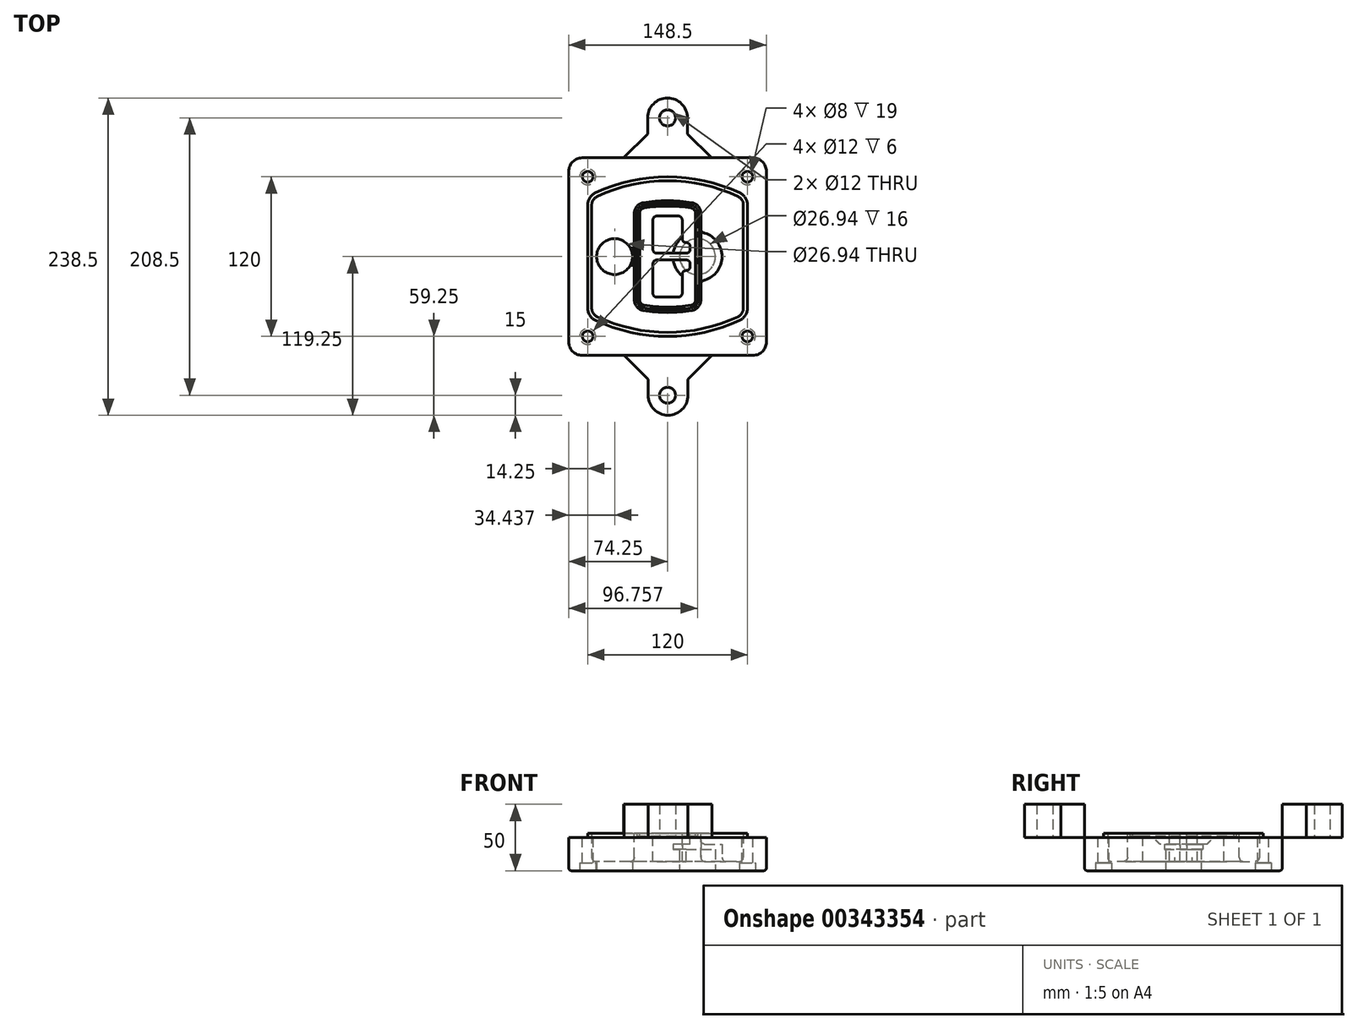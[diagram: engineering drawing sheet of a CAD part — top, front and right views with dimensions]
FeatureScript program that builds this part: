
annotation { "Feature Type Name" : "Feature", "Feature Type Description" : "" }
export const myFeature = defineFeature(function(context is Context, id is Id, definition is map)
    precondition{}
    {
        {
            var Q0;
            Q0=qCreatedBy(makeId("Top.planeOp"),FACE);
            var sketch = newSketch(context, id + "F0", { "sketchPlane" : qUnion([Q0])});
            skPoint(sketch, "E0.rect.middle", {"position": v(0, 0) * mm});
            skLineSegment(sketch, "E1.bottom", {"start": v(-64.25, -74.25) * mm, "end": v(64.25, -74.25) * mm});
            skLineSegment(sketch, "E1.top", {"start": v(-64.25, 74.25) * mm, "end": v(64.25, 74.25) * mm});
            skLineSegment(sketch, "E1.left", {"start": v(-74.25, -64.25) * mm, "end": v(-74.25, 64.25) * mm});
            skLineSegment(sketch, "E1.right", {"start": v(74.25, -64.25) * mm, "end": v(74.25, 64.25) * mm});
            skLineSegment(sketch, "E2", {"start": v(-74.25, 74.25) * mm, "end": v(74.25, -74.25) * mm, "construction": true});
            skLineSegment(sketch, "E3", {"start": v(74.25, 74.25) * mm, "end": v(-74.25, -74.25) * mm, "construction": true});
            skCircle(sketch, "E4", {"center": v(-60, 60) * mm, "radius": 4 * mm});
            skCircle(sketch, "E5", {"center": v(60, 60) * mm, "radius": 4 * mm});
            skCircle(sketch, "E6", {"center": v(60, -60) * mm, "radius": 4 * mm});
            skCircle(sketch, "E7", {"center": v(-60, -60) * mm, "radius": 4 * mm});
            skLineSegment(sketch, "E8", {"start": v(-60, 60) * mm, "end": v(60, 60) * mm, "construction": true});
            skLineSegment(sketch, "E9", {"start": v(60, 60) * mm, "end": v(60, -60) * mm, "construction": true});
            skLineSegment(sketch, "E10", {"start": v(60, -60) * mm, "end": v(-60, -60) * mm, "construction": true});
            skLineSegment(sketch, "E11", {"start": v(-60, -60) * mm, "end": v(-60, 60) * mm, "construction": true});
            skLineSegment(sketch, "E12", {"start": v(-60, 38.83) * mm, "end": v(-60, -38.83) * mm});
            skLineSegment(sketch, "E13", {"start": v(60, 38.83) * mm, "end": v(60, -38.83) * mm});
            skArc(sketch, "E14", {"start": v(54.26, 47.88) * mm, "mid": v(0, 60) * mm, "end": v(-54.26, 47.88) * mm});
            skArc(sketch, "E15", {"start": v(-54.26, -47.88) * mm, "mid": v(0, -60) * mm, "end": v(54.26, -47.88) * mm});
            skLineSegment(sketch, "E16", {"start": v(-60, 0) * mm, "end": v(60, 0) * mm, "construction": true});
            skPoint(sketch, "E17.visualSharp", {"position": v(-60, -45) * mm});
            skArc(sketch, "E17.filletArc", {"start": v(-60, -38.83) * mm, "mid": v(-58.44, -44.2) * mm, "end": v(-54.26, -47.88) * mm});
            skPoint(sketch, "E18.visualSharp", {"position": v(-60, 45) * mm});
            skArc(sketch, "E18.filletArc", {"start": v(-54.26, 47.88) * mm, "mid": v(-58.44, 44.2) * mm, "end": v(-60, 38.83) * mm});
            skPoint(sketch, "E19.visualSharp", {"position": v(60, 45) * mm});
            skArc(sketch, "E19.filletArc", {"start": v(60, 38.83) * mm, "mid": v(58.44, 44.2) * mm, "end": v(54.26, 47.88) * mm});
            skPoint(sketch, "E20.visualSharp", {"position": v(60, -45) * mm});
            skArc(sketch, "E20.filletArc", {"start": v(54.26, -47.88) * mm, "mid": v(58.44, -44.2) * mm, "end": v(60, -38.83) * mm});
            skPoint(sketch, "E21.visualSharp", {"position": v(-74.25, 74.25) * mm});
            skArc(sketch, "E21.filletArc", {"start": v(-64.25, 74.25) * mm, "mid": v(-71.32, 71.32) * mm, "end": v(-74.25, 64.25) * mm});
            skPoint(sketch, "E22.visualSharp", {"position": v(74.25, 74.25) * mm});
            skArc(sketch, "E22.filletArc", {"start": v(74.25, 64.25) * mm, "mid": v(71.32, 71.32) * mm, "end": v(64.25, 74.25) * mm});
            skPoint(sketch, "E23.visualSharp", {"position": v(74.25, -74.25) * mm});
            skArc(sketch, "E23.filletArc", {"start": v(64.25, -74.25) * mm, "mid": v(71.32, -71.32) * mm, "end": v(74.25, -64.25) * mm});
            skPoint(sketch, "E24.visualSharp", {"position": v(-74.25, -74.25) * mm});
            skArc(sketch, "E24.filletArc", {"start": v(-74.25, -64.25) * mm, "mid": v(-71.32, -71.32) * mm, "end": v(-64.25, -74.25) * mm});
            skArc(sketch, "E25.0", {"start": v(57, 38.83) * mm, "mid": v(55.9, 42.58) * mm, "end": v(52.98, 45.17) * mm});
            skLineSegment(sketch, "E25.1", {"start": v(57, 38.83) * mm, "end": v(57, -38.83) * mm});
            skArc(sketch, "E25.2", {"start": v(52.98, -45.17) * mm, "mid": v(55.9, -42.58) * mm, "end": v(57, -38.83) * mm});
            skArc(sketch, "E25.3", {"start": v(-52.98, -45.17) * mm, "mid": v(0, -57) * mm, "end": v(52.98, -45.17) * mm});
            skArc(sketch, "E25.4", {"start": v(-57, -38.83) * mm, "mid": v(-55.9, -42.58) * mm, "end": v(-52.98, -45.17) * mm});
            skArc(sketch, "E25.5", {"start": v(52.98, 45.17) * mm, "mid": v(0, 57) * mm, "end": v(-52.98, 45.17) * mm});
            skLineSegment(sketch, "E25.6", {"start": v(-57, 38.83) * mm, "end": v(-57, -38.83) * mm});
            skArc(sketch, "E25.7", {"start": v(-52.98, 45.17) * mm, "mid": v(-55.9, 42.58) * mm, "end": v(-57, 38.83) * mm});
            skArc(sketch, "E26.0", {"start": v(-55.96, 51.5) * mm, "mid": v(-61.82, 46.33) * mm, "end": v(-64, 38.83) * mm});
            skArc(sketch, "E26.1", {"start": v(55.96, 51.5) * mm, "mid": v(0, 64) * mm, "end": v(-55.96, 51.5) * mm});
            skArc(sketch, "E26.2", {"start": v(64, 38.83) * mm, "mid": v(61.82, 46.33) * mm, "end": v(55.96, 51.5) * mm});
            skLineSegment(sketch, "E26.3", {"start": v(64, 38.83) * mm, "end": v(64, -38.83) * mm});
            skArc(sketch, "E26.4", {"start": v(55.96, -51.5) * mm, "mid": v(61.82, -46.33) * mm, "end": v(64, -38.83) * mm});
            skLineSegment(sketch, "E26.5", {"start": v(-64, 38.83) * mm, "end": v(-64, -38.83) * mm});
            skArc(sketch, "E26.6", {"start": v(-55.96, -51.5) * mm, "mid": v(0, -64) * mm, "end": v(55.96, -51.5) * mm});
            skArc(sketch, "E26.7", {"start": v(-64, -38.83) * mm, "mid": v(-61.82, -46.33) * mm, "end": v(-55.96, -51.5) * mm});
            skSolve(sketch);
        }
        {
            var Q0;
            Q0=makeQuery(id+"F0.imprint","IMPRINT",FACE,{"disambiguationData":[TD([[makeQuery(id+"F0.imprint","IMPRINT",EDGE,{"derivedFrom":sQuery(id+"F0.wireOp",EDGE,"E1.bottom")}),1.0]])]});
            var Q1;
            Q1=makeQuery(id+"F0.imprint","IMPRINT",FACE,{"disambiguationData":[TD([[makeQuery(id+"F0.imprint","IMPRINT",EDGE,{"derivedFrom":sQuery(id+"F0.wireOp",EDGE,"E12")}),1.0]])]});
            var Q2;
            Q2=makeQuery(id+"F0.imprint","IMPRINT",FACE,{"disambiguationData":[TD([[makeQuery(id+"F0.imprint","IMPRINT",EDGE,{"derivedFrom":sQuery(id+"F0.wireOp",EDGE,"E25.0")}),1.0]])]});
            var Q3;
            Q3=makeQuery(id+"F0.imprint","IMPRINT",FACE,{"disambiguationData":[TD([[makeQuery(id+"F0.imprint","IMPRINT",EDGE,{"derivedFrom":sQuery(id+"F0.wireOp",EDGE,"E12")}),-1.0]])]});
            extrude(context, id + "F1", {"entities" : qUnion([Q0, Q1, Q2, Q3]), "oppositeDirection" : true, "depth" : 25 * mm});
        }
        {
            var Q0;
            Q0=makeQuery(id+"F0.imprint","IMPRINT",FACE,{"disambiguationData":[TD([[makeQuery(id+"F0.imprint","IMPRINT",EDGE,{"derivedFrom":sQuery(id+"F0.wireOp",EDGE,"E12")}),1.0]])]});
            extrude(context, id + "F2", {"entities" : qUnion([Q0]), "operationType" : NewBodyOperationType.ADD, "depth" : 3 * mm});
        }
        {
            var Q0;
            Q0=makeQuery(id+"F0.imprint","IMPRINT",FACE,{"disambiguationData":[TD([[makeQuery(id+"F0.imprint","IMPRINT",EDGE,{"derivedFrom":sQuery(id+"F0.wireOp",EDGE,"E25.0")}),1.0]])]});
            extrude(context, id + "F3", {"entities" : qUnion([Q0]), "operationType" : NewBodyOperationType.REMOVE, "oppositeDirection" : true, "depth" : 18 * mm});
        }
        {
            var Q0;
            Q0=makeQuery(id+"F2.opExtrude","CAP_FACE",FACE,{"disambiguationData":[OSD([sQuery(id+"F0.wireOp",EDGE,"E12"),sQuery(id+"F0.wireOp",EDGE,"E13"),sQuery(id+"F0.wireOp",EDGE,"E14"),sQuery(id+"F0.wireOp",EDGE,"E15"),sQuery(id+"F0.wireOp",EDGE,"E17.filletArc"),sQuery(id+"F0.wireOp",EDGE,"E18.filletArc"),sQuery(id+"F0.wireOp",EDGE,"E19.filletArc"),sQuery(id+"F0.wireOp",EDGE,"E20.filletArc"),sQuery(id+"F0.wireOp",EDGE,"E25.0"),sQuery(id+"F0.wireOp",EDGE,"E25.1"),sQuery(id+"F0.wireOp",EDGE,"E25.2"),sQuery(id+"F0.wireOp",EDGE,"E25.3"),sQuery(id+"F0.wireOp",EDGE,"E25.4"),sQuery(id+"F0.wireOp",EDGE,"E25.5"),sQuery(id+"F0.wireOp",EDGE,"E25.6"),sQuery(id+"F0.wireOp",EDGE,"E25.7")])],"isStart":false});
            var sketch = newSketch(context, id + "F4", { "sketchPlane" : qUnion([Q0])});
            skArc(sketch, "E27.0", {"start": v(-18.34, -40.45) * mm, "mid": v(0, -42) * mm, "end": v(18.34, -40.45) * mm});
            skArc(sketch, "E28.0", {"start": v(18.34, 40.45) * mm, "mid": v(0, 42) * mm, "end": v(-18.34, 40.45) * mm});
            skLineSegment(sketch, "E29", {"start": v(-25, 32.57) * mm, "end": v(-25, -32.57) * mm});
            skLineSegment(sketch, "E30", {"start": v(25, 32.57) * mm, "end": v(25, -32.57) * mm});
            skLineSegment(sketch, "E31", {"start": v(-25, 39.1) * mm, "end": v(25, 39.1) * mm, "construction": true});
            skLineSegment(sketch, "E32", {"start": v(-25, -39.1) * mm, "end": v(25, -39.1) * mm, "construction": true});
            skPoint(sketch, "E33.visualSharp", {"position": v(-25, 39.1) * mm});
            skArc(sketch, "E33.filletArc", {"start": v(-18.34, 40.45) * mm, "mid": v(-23.11, 37.73) * mm, "end": v(-25, 32.57) * mm});
            skPoint(sketch, "E34.visualSharp", {"position": v(25, 39.1) * mm});
            skArc(sketch, "E34.filletArc", {"start": v(25, 32.57) * mm, "mid": v(23.11, 37.73) * mm, "end": v(18.34, 40.45) * mm});
            skPoint(sketch, "E35.visualSharp", {"position": v(25, -39.1) * mm});
            skArc(sketch, "E35.filletArc", {"start": v(18.34, -40.45) * mm, "mid": v(23.11, -37.73) * mm, "end": v(25, -32.57) * mm});
            skPoint(sketch, "E36.visualSharp", {"position": v(-25, -39.1) * mm});
            skArc(sketch, "E36.filletArc", {"start": v(-25, -32.57) * mm, "mid": v(-23.11, -37.73) * mm, "end": v(-18.34, -40.45) * mm});
            skArc(sketch, "E37.0", {"start": v(52.98, 45.17) * mm, "mid": v(0, 57) * mm, "end": v(-52.98, 45.17) * mm});
            skArc(sketch, "E37.1", {"start": v(-52.98, 45.17) * mm, "mid": v(-55.9, 42.58) * mm, "end": v(-57, 38.83) * mm});
            skLineSegment(sketch, "E37.2", {"start": v(-57, 38.83) * mm, "end": v(-57, -38.83) * mm});
            skArc(sketch, "E37.3", {"start": v(-57, -38.83) * mm, "mid": v(-55.9, -42.58) * mm, "end": v(-52.98, -45.17) * mm});
            skArc(sketch, "E37.4", {"start": v(-52.98, -45.17) * mm, "mid": v(0, -57) * mm, "end": v(52.98, -45.17) * mm});
            skArc(sketch, "E37.5", {"start": v(52.98, -45.17) * mm, "mid": v(55.9, -42.58) * mm, "end": v(57, -38.83) * mm});
            skLineSegment(sketch, "E37.6", {"start": v(57, 38.83) * mm, "end": v(57, -38.83) * mm});
            skArc(sketch, "E37.7", {"start": v(57, 38.83) * mm, "mid": v(55.9, 42.58) * mm, "end": v(52.98, 45.17) * mm});
            skLineSegment(sketch, "E38.0", {"start": v(23, 32.57) * mm, "end": v(23, -32.57) * mm});
            skArc(sketch, "E38.1", {"start": v(18, -38.48) * mm, "mid": v(21.58, -36.44) * mm, "end": v(23, -32.57) * mm});
            skArc(sketch, "E38.2", {"start": v(-18, -38.48) * mm, "mid": v(0, -40) * mm, "end": v(18, -38.48) * mm});
            skArc(sketch, "E38.3", {"start": v(-23, -32.57) * mm, "mid": v(-21.58, -36.44) * mm, "end": v(-18, -38.48) * mm});
            skLineSegment(sketch, "E38.4", {"start": v(-23, 32.57) * mm, "end": v(-23, -32.57) * mm});
            skArc(sketch, "E38.5", {"start": v(23, 32.57) * mm, "mid": v(21.58, 36.44) * mm, "end": v(18, 38.48) * mm});
            skArc(sketch, "E38.6", {"start": v(-18, 38.48) * mm, "mid": v(-21.58, 36.44) * mm, "end": v(-23, 32.57) * mm});
            skArc(sketch, "E38.7", {"start": v(18, 38.48) * mm, "mid": v(0, 40) * mm, "end": v(-18, 38.48) * mm});
            skArc(sketch, "E39.0", {"start": v(21, 32.57) * mm, "mid": v(20.06, 35.15) * mm, "end": v(17.67, 36.5) * mm});
            skLineSegment(sketch, "E39.1", {"start": v(21, 32.57) * mm, "end": v(21, -32.57) * mm});
            skArc(sketch, "E39.2", {"start": v(17.67, -36.5) * mm, "mid": v(20.06, -35.15) * mm, "end": v(21, -32.57) * mm});
            skArc(sketch, "E39.3", {"start": v(-17.67, -36.5) * mm, "mid": v(0, -38) * mm, "end": v(17.67, -36.5) * mm});
            skArc(sketch, "E39.4", {"start": v(-21, -32.57) * mm, "mid": v(-20.06, -35.15) * mm, "end": v(-17.67, -36.5) * mm});
            skArc(sketch, "E39.5", {"start": v(17.67, 36.5) * mm, "mid": v(0, 38) * mm, "end": v(-17.67, 36.5) * mm});
            skLineSegment(sketch, "E39.6", {"start": v(-21, 32.57) * mm, "end": v(-21, -32.57) * mm});
            skArc(sketch, "E39.7", {"start": v(-17.67, 36.5) * mm, "mid": v(-20.06, 35.15) * mm, "end": v(-21, 32.57) * mm});
            skLineSegment(sketch, "E40", {"start": v(-25, 0) * mm, "end": v(25, 0) * mm, "construction": true});
            skLineSegment(sketch, "E41", {"start": v(-11, 5.5) * mm, "end": v(-11, 27.5) * mm});
            skLineSegment(sketch, "E42", {"start": v(-8, 30.5) * mm, "end": v(8, 30.5) * mm});
            skLineSegment(sketch, "E43", {"start": v(11, 27.5) * mm, "end": v(11, 13.5) * mm});
            skLineSegment(sketch, "E44", {"start": v(14, 10.5) * mm, "end": v(14, 10.5) * mm});
            skLineSegment(sketch, "E45", {"start": v(17, 7.5) * mm, "end": v(17, 5.5) * mm});
            skLineSegment(sketch, "E46", {"start": v(14, 2.5) * mm, "end": v(-8, 2.5) * mm});
            skPoint(sketch, "E47.visualSharp", {"position": v(-11, 30.5) * mm});
            skArc(sketch, "E47.filletArc", {"start": v(-8, 30.5) * mm, "mid": v(-10.12, 29.62) * mm, "end": v(-11, 27.5) * mm});
            skPoint(sketch, "E48.visualSharp", {"position": v(11, 30.5) * mm});
            skArc(sketch, "E48.filletArc", {"start": v(11, 27.5) * mm, "mid": v(10.12, 29.62) * mm, "end": v(8, 30.5) * mm});
            skPoint(sketch, "E49.visualSharp", {"position": v(11, 10.5) * mm});
            skArc(sketch, "E49.filletArc", {"start": v(11, 13.5) * mm, "mid": v(11.88, 11.38) * mm, "end": v(14, 10.5) * mm});
            skPoint(sketch, "E50.visualSharp", {"position": v(17, 10.5) * mm});
            skArc(sketch, "E50.filletArc", {"start": v(17, 7.5) * mm, "mid": v(16.12, 9.62) * mm, "end": v(14, 10.5) * mm});
            skPoint(sketch, "E51.visualSharp", {"position": v(17, 2.5) * mm});
            skArc(sketch, "E51.filletArc", {"start": v(14, 2.5) * mm, "mid": v(16.12, 3.38) * mm, "end": v(17, 5.5) * mm});
            skPoint(sketch, "E52.visualSharp", {"position": v(-11, 2.5) * mm});
            skArc(sketch, "E52.filletArc", {"start": v(-11, 5.5) * mm, "mid": v(-10.12, 3.38) * mm, "end": v(-8, 2.5) * mm});
            skLineSegment(sketch, "E53.0.MirrorCS", {"start": v(14, -2.5) * mm, "end": v(-8, -2.5) * mm});
            skArc(sketch, "E54.0.MirrorCS", {"start": v(-11, -5.5) * mm, "mid": v(-10.12, -3.38) * mm, "end": v(-8, -2.5) * mm});
            skLineSegment(sketch, "E55.0.MirrorCS", {"start": v(-11, -5.5) * mm, "end": v(-11, -27.5) * mm});
            skArc(sketch, "E56.0.MirrorCS", {"start": v(-8, -30.5) * mm, "mid": v(-10.12, -29.62) * mm, "end": v(-11, -27.5) * mm});
            skLineSegment(sketch, "E57.0.MirrorCS", {"start": v(-8, -30.5) * mm, "end": v(8, -30.5) * mm});
            skArc(sketch, "E58.0.MirrorCS", {"start": v(11, -27.5) * mm, "mid": v(10.12, -29.62) * mm, "end": v(8, -30.5) * mm});
            skLineSegment(sketch, "E59.0.MirrorCS", {"start": v(11, -27.5) * mm, "end": v(11, -13.5) * mm});
            skArc(sketch, "E60.0.MirrorCS", {"start": v(11, -13.5) * mm, "mid": v(11.88, -11.38) * mm, "end": v(14, -10.5) * mm});
            skArc(sketch, "E61.0.MirrorCS", {"start": v(17, -7.5) * mm, "mid": v(16.12, -9.62) * mm, "end": v(14, -10.5) * mm});
            skLineSegment(sketch, "E62.0.MirrorCS", {"start": v(17, -7.5) * mm, "end": v(17, -5.5) * mm});
            skArc(sketch, "E63.0.MirrorCS", {"start": v(14, -2.5) * mm, "mid": v(16.12, -3.38) * mm, "end": v(17, -5.5) * mm});
            skSolve(sketch);
        }
        {
            var Q0;
            Q0=makeQuery(id+"F4.imprint","IMPRINT",FACE,{"disambiguationData":[TD([[makeQuery(id+"F4.imprint","IMPRINT",EDGE,{"derivedFrom":sQuery(id+"F4.wireOp",EDGE,"E27.0")}),1.0]])]});
            var Q1;
            Q1=makeQuery(id+"F4.imprint","IMPRINT",FACE,{"disambiguationData":[TD([[makeQuery(id+"F4.imprint","IMPRINT",EDGE,{"derivedFrom":sQuery(id+"F4.wireOp",EDGE,"E38.0")}),-1.0]])]});
            var Q2;
            Q2=makeQuery(id+"F4.imprint","IMPRINT",FACE,{"disambiguationData":[TD([[makeQuery(id+"F4.imprint","IMPRINT",EDGE,{"derivedFrom":sQuery(id+"F4.wireOp",EDGE,"E39.0")}),1.0]])]});
            extrude(context, id + "F5", {"entities" : qUnion([Q0, Q1, Q2]), "operationType" : NewBodyOperationType.ADD, "endBound" : BoundingType.UP_TO_NEXT, "oppositeDirection" : true, "depth" : 25 * mm});
        }
        {
            var Q0;
            Q0=makeQuery(id+"F4.imprint","IMPRINT",FACE,{"disambiguationData":[TD([[makeQuery(id+"F4.imprint","IMPRINT",EDGE,{"derivedFrom":sQuery(id+"F4.wireOp",EDGE,"E38.0")}),-1.0]])]});
            extrude(context, id + "F6", {"entities" : qUnion([Q0]), "operationType" : NewBodyOperationType.REMOVE, "oppositeDirection" : true, "depth" : 2 * mm});
        }
        {
            var Q0;
            Q0=makeQuery(id+"F1.opExtrude","CAP_FACE",FACE,{"disambiguationData":[OSD([sQuery(id+"F0.wireOp",EDGE,"E1.bottom"),sQuery(id+"F0.wireOp",EDGE,"E1.top"),sQuery(id+"F0.wireOp",EDGE,"E1.left"),sQuery(id+"F0.wireOp",EDGE,"E1.right"),sQuery(id+"F0.wireOp",EDGE,"E4"),sQuery(id+"F0.wireOp",EDGE,"E5"),sQuery(id+"F0.wireOp",EDGE,"E6"),sQuery(id+"F0.wireOp",EDGE,"E7"),sQuery(id+"F0.wireOp",EDGE,"E21.filletArc"),sQuery(id+"F0.wireOp",EDGE,"E22.filletArc"),sQuery(id+"F0.wireOp",EDGE,"E23.filletArc"),sQuery(id+"F0.wireOp",EDGE,"E24.filletArc")])],"isStart":false});
            var sketch = newSketch(context, id + "F7", { "sketchPlane" : qUnion([Q0])});
            skCircle(sketch, "E64", {"center": v(22.5, 0) * mm, "radius": 13.47 * mm});
            skCircle(sketch, "E65", {"center": v(-39.81, 0) * mm, "radius": 13.47 * mm});
            skLineSegment(sketch, "E66", {"start": v(74.25, 0) * mm, "end": v(-74.25, 0) * mm});
            skCircle(sketch, "E67", {"center": v(22.5, 0) * mm, "radius": 18.47 * mm});
            skCircle(sketch, "E68", {"center": v(60, -60) * mm, "radius": 6 * mm});
            skCircle(sketch, "E69", {"center": v(-60, -60) * mm, "radius": 6 * mm});
            skCircle(sketch, "E70", {"center": v(-60, 60) * mm, "radius": 6 * mm});
            skCircle(sketch, "E71", {"center": v(60, 60) * mm, "radius": 6 * mm});
            skSolve(sketch);
        }
        {
            var Q0;
            {var subQ1=sQuery(id+"F7.wireOp",EDGE,"E66");var subQ4=sQuery(id+"F7.wireOp",EDGE,"E64");var subQ6=makeQuery(id+"F7.imprint","INTERSECT",VERTEX,{"disambiguationData":[OD(0.0)],"derivedFrom":[subQ4,subQ1]});Q0=makeQuery(id+"F7.imprint","IMPRINT",FACE,{"disambiguationData":[TD([[makeQuery(id+"F7.imprint","IMPRINT",EDGE,{"disambiguationData":[TD([[subQ6,-1.0]])],"derivedFrom":subQ4}),-1.0]])]});}
            var Q1;
            {var subQ0=sQuery(id+"F7.wireOp",EDGE,"E66");var subQ1=sQuery(id+"F7.wireOp",EDGE,"E64");var subQ3=makeQuery(id+"F7.imprint","INTERSECT",VERTEX,{"disambiguationData":[OD(0.0)],"derivedFrom":[subQ1,subQ0]});Q1=makeQuery(id+"F7.imprint","IMPRINT",FACE,{"disambiguationData":[TD([[makeQuery(id+"F7.imprint","IMPRINT",EDGE,{"disambiguationData":[TD([[subQ3,-1.0]])],"derivedFrom":subQ1}),1.0]])]});}
            var Q2;
            {var subQ0=sQuery(id+"F7.wireOp",EDGE,"E66");var subQ1=sQuery(id+"F7.wireOp",EDGE,"E64");var subQ3=makeQuery(id+"F7.imprint","INTERSECT",VERTEX,{"disambiguationData":[OD(0.0)],"derivedFrom":[subQ1,subQ0]});Q2=makeQuery(id+"F7.imprint","IMPRINT",FACE,{"disambiguationData":[TD([[makeQuery(id+"F7.imprint","IMPRINT",EDGE,{"disambiguationData":[TD([[subQ3,1.0]])],"derivedFrom":subQ1}),1.0]])]});}
            var Q3;
            {var subQ1=sQuery(id+"F7.wireOp",EDGE,"E66");var subQ4=sQuery(id+"F7.wireOp",EDGE,"E64");var subQ6=makeQuery(id+"F7.imprint","INTERSECT",VERTEX,{"disambiguationData":[OD(0.0)],"derivedFrom":[subQ4,subQ1]});Q3=makeQuery(id+"F7.imprint","IMPRINT",FACE,{"disambiguationData":[TD([[makeQuery(id+"F7.imprint","IMPRINT",EDGE,{"disambiguationData":[TD([[subQ6,1.0]])],"derivedFrom":subQ4}),-1.0]])]});}
            extrude(context, id + "F8", {"entities" : qUnion([Q0, Q1, Q2, Q3]), "operationType" : NewBodyOperationType.ADD, "oppositeDirection" : true, "depth" : 20 * mm});
        }
        {
            var Q0;
            {var subQ0=sQuery(id+"F7.wireOp",EDGE,"E66");var subQ1=sQuery(id+"F7.wireOp",EDGE,"E64");var subQ3=makeQuery(id+"F7.imprint","INTERSECT",VERTEX,{"disambiguationData":[OD(0.0)],"derivedFrom":[subQ1,subQ0]});Q0=makeQuery(id+"F7.imprint","IMPRINT",FACE,{"disambiguationData":[TD([[makeQuery(id+"F7.imprint","IMPRINT",EDGE,{"disambiguationData":[TD([[subQ3,-1.0]])],"derivedFrom":subQ1}),1.0]])]});}
            var Q1;
            {var subQ0=sQuery(id+"F7.wireOp",EDGE,"E66");var subQ1=sQuery(id+"F7.wireOp",EDGE,"E64");var subQ3=makeQuery(id+"F7.imprint","INTERSECT",VERTEX,{"disambiguationData":[OD(0.0)],"derivedFrom":[subQ1,subQ0]});Q1=makeQuery(id+"F7.imprint","IMPRINT",FACE,{"disambiguationData":[TD([[makeQuery(id+"F7.imprint","IMPRINT",EDGE,{"disambiguationData":[TD([[subQ3,1.0]])],"derivedFrom":subQ1}),1.0]])]});}
            extrude(context, id + "F9", {"entities" : qUnion([Q0, Q1]), "operationType" : NewBodyOperationType.REMOVE, "oppositeDirection" : true, "depth" : 16 * mm});
        }
        {
            var Q0;
            {var subQ0=sQuery(id+"F7.wireOp",EDGE,"E66");var subQ1=sQuery(id+"F7.wireOp",EDGE,"E65");var subQ3=makeQuery(id+"F7.imprint","INTERSECT",VERTEX,{"disambiguationData":[OD(0.0)],"derivedFrom":[subQ1,subQ0]});Q0=makeQuery(id+"F7.imprint","IMPRINT",FACE,{"disambiguationData":[TD([[makeQuery(id+"F7.imprint","IMPRINT",EDGE,{"disambiguationData":[TD([[subQ3,-1.0]])],"derivedFrom":subQ1}),1.0]])]});}
            var Q1;
            {var subQ0=sQuery(id+"F7.wireOp",EDGE,"E66");var subQ1=sQuery(id+"F7.wireOp",EDGE,"E65");var subQ3=makeQuery(id+"F7.imprint","INTERSECT",VERTEX,{"disambiguationData":[OD(0.0)],"derivedFrom":[subQ1,subQ0]});Q1=makeQuery(id+"F7.imprint","IMPRINT",FACE,{"disambiguationData":[TD([[makeQuery(id+"F7.imprint","IMPRINT",EDGE,{"disambiguationData":[TD([[subQ3,1.0]])],"derivedFrom":subQ1}),1.0]])]});}
            extrude(context, id + "F10", {"entities" : qUnion([Q0, Q1]), "operationType" : NewBodyOperationType.REMOVE, "oppositeDirection" : true, "depth" : 25 * mm});
        }
        {
            var Q0;
            Q0=makeQuery(id+"F7.imprint","IMPRINT",FACE,{"disambiguationData":[TD([[makeQuery(id+"F7.imprint","IMPRINT",EDGE,{"derivedFrom":sQuery(id+"F7.wireOp",EDGE,"E68")}),1.0]])]});
            var Q1;
            Q1=makeQuery(id+"F7.imprint","IMPRINT",FACE,{"disambiguationData":[TD([[makeQuery(id+"F7.imprint","IMPRINT",EDGE,{"derivedFrom":makeQuery(id+"F1.opExtrude","CAP_EDGE",EDGE,{"disambiguationData":[OSD([sQuery(id+"F0.wireOp",EDGE,"E5")])],"isStart":false})}),-1.0]])]});
            var Q2;
            Q2=makeQuery(id+"F7.imprint","IMPRINT",FACE,{"disambiguationData":[TD([[makeQuery(id+"F7.imprint","IMPRINT",EDGE,{"derivedFrom":sQuery(id+"F7.wireOp",EDGE,"E69")}),1.0]])]});
            var Q3;
            Q3=makeQuery(id+"F7.imprint","IMPRINT",FACE,{"disambiguationData":[TD([[makeQuery(id+"F7.imprint","IMPRINT",EDGE,{"derivedFrom":makeQuery(id+"F1.opExtrude","CAP_EDGE",EDGE,{"disambiguationData":[OSD([sQuery(id+"F0.wireOp",EDGE,"E4")])],"isStart":false})}),-1.0]])]});
            var Q4;
            Q4=makeQuery(id+"F7.imprint","IMPRINT",FACE,{"disambiguationData":[TD([[makeQuery(id+"F7.imprint","IMPRINT",EDGE,{"derivedFrom":sQuery(id+"F7.wireOp",EDGE,"E70")}),1.0]])]});
            var Q5;
            Q5=makeQuery(id+"F7.imprint","IMPRINT",FACE,{"disambiguationData":[TD([[makeQuery(id+"F7.imprint","IMPRINT",EDGE,{"derivedFrom":makeQuery(id+"F1.opExtrude","CAP_EDGE",EDGE,{"disambiguationData":[OSD([sQuery(id+"F0.wireOp",EDGE,"E7")])],"isStart":false})}),-1.0]])]});
            var Q6;
            Q6=makeQuery(id+"F7.imprint","IMPRINT",FACE,{"disambiguationData":[TD([[makeQuery(id+"F7.imprint","IMPRINT",EDGE,{"derivedFrom":sQuery(id+"F7.wireOp",EDGE,"E71")}),1.0]])]});
            var Q7;
            Q7=makeQuery(id+"F7.imprint","IMPRINT",FACE,{"disambiguationData":[TD([[makeQuery(id+"F7.imprint","IMPRINT",EDGE,{"derivedFrom":makeQuery(id+"F1.opExtrude","CAP_EDGE",EDGE,{"disambiguationData":[OSD([sQuery(id+"F0.wireOp",EDGE,"E6")])],"isStart":false})}),-1.0]])]});
            extrude(context, id + "F11", {"entities" : qUnion([Q0, Q1, Q2, Q3, Q4, Q5, Q6, Q7]), "operationType" : NewBodyOperationType.REMOVE, "oppositeDirection" : true, "depth" : 6 * mm});
        }
        {
            var Q0;
            Q0=makeQuery(id+"F9.boolean.opBoolean","COPY",FACE,{"derivedFrom":makeQuery(id+"F9.opExtrude","CAP_FACE",FACE,{"disambiguationData":[OSD([sQuery(id+"F7.wireOp",EDGE,"E64")])],"isStart":false})});
            var sketch = newSketch(context, id + "F12", { "sketchPlane" : qUnion([Q0])});
            skArc(sketch, "E72.0", {"start": v(11, 14.45) * mm, "mid": v(6.45, 9.13) * mm, "end": v(4.2, 2.5) * mm});
            skArc(sketch, "E72.1", {"start": v(4.2, -2.5) * mm, "mid": v(6.45, -9.13) * mm, "end": v(11, -14.45) * mm});
            skLineSegment(sketch, "E73", {"start": v(4.2, -2.5) * mm, "end": v(14, -2.5) * mm});
            skLineSegment(sketch, "E74.0", {"start": v(14, 2.5) * mm, "end": v(4.2, 2.5) * mm});
            skArc(sketch, "E74.1", {"start": v(14, 2.5) * mm, "mid": v(16.12, 3.38) * mm, "end": v(17, 5.5) * mm});
            skLineSegment(sketch, "E74.2", {"start": v(17, 7.5) * mm, "end": v(17, 5.5) * mm});
            skArc(sketch, "E74.3", {"start": v(17, 7.5) * mm, "mid": v(16.12, 9.62) * mm, "end": v(14, 10.5) * mm});
            skArc(sketch, "E74.4", {"start": v(11, 13.5) * mm, "mid": v(11.88, 11.38) * mm, "end": v(14, 10.5) * mm});
            skLineSegment(sketch, "E74.5", {"start": v(11, 14.45) * mm, "end": v(11, 13.5) * mm});
            skLineSegment(sketch, "E74.7", {"start": v(14, -2.5) * mm, "end": v(4.2, -2.5) * mm});
            skArc(sketch, "E74.8", {"start": v(14, -2.5) * mm, "mid": v(16.12, -3.38) * mm, "end": v(17, -5.5) * mm});
            skLineSegment(sketch, "E74.9", {"start": v(17, -7.5) * mm, "end": v(17, -5.5) * mm});
            skArc(sketch, "E74.10", {"start": v(17, -7.5) * mm, "mid": v(16.12, -9.62) * mm, "end": v(14, -10.5) * mm});
            skArc(sketch, "E74.11", {"start": v(11, -13.5) * mm, "mid": v(11.88, -11.38) * mm, "end": v(14, -10.5) * mm});
            skLineSegment(sketch, "E74.12", {"start": v(11, -14.45) * mm, "end": v(11, -13.5) * mm});
            skPoint(sketch, "E75.orphan", {"position": v(11, -27.5) * mm});
            skPoint(sketch, "E76.orphan", {"position": v(-8, -2.5) * mm});
            skPoint(sketch, "E77.orphan", {"position": v(-8, 2.5) * mm});
            skPoint(sketch, "E78.orphan", {"position": v(11, 27.5) * mm});
            skSolve(sketch);
        }
        {
            var Q0;
            {var subQ7=sQuery(id+"F12.wireOp",EDGE,"E72.0");var subQ14=sQuery(id+"F12.wireOp",EDGE,"E72.1");var subQ16=sQuery(id+"F12.wireOp",EDGE,"E74.1");var subQ18=sQuery(id+"F12.wireOp",EDGE,"E74.8");Q0=qUnion([makeQuery(id+"F12.imprint","IMPRINT",FACE,{"disambiguationData":[TD([[makeQuery(id+"F12.imprint","IMPRINT",EDGE,{"derivedFrom":subQ7}),1.0]])]}),makeQuery(id+"F12.imprint","IMPRINT",FACE,{"disambiguationData":[TD([[makeQuery(id+"F12.imprint","IMPRINT",EDGE,{"derivedFrom":subQ14}),1.0]])]}),makeQuery(id+"F12.imprint","IMPRINT",FACE,{"disambiguationData":[TD([[makeQuery(id+"F12.imprint","IMPRINT",EDGE,{"derivedFrom":subQ16}),1.0]])]}),makeQuery(id+"F12.imprint","IMPRINT",FACE,{"disambiguationData":[TD([[makeQuery(id+"F12.imprint","IMPRINT",EDGE,{"derivedFrom":subQ18}),-1.0]])]})]);}
            var Q1;
            Q1=makeQuery(id+"F5.boolean.opBoolean","SPLIT",FACE,{"disambiguationData":[TD([makeQuery(id+"F5.opExtrude","SWEPT_FACE",FACE,{"disambiguationData":[OSD([sQuery(id+"F4.wireOp",EDGE,"E41")])]})])],"derivedFrom":makeQuery(id+"F3.boolean.opBoolean","COPY",FACE,{"derivedFrom":makeQuery(id+"F3.opExtrude","CAP_FACE",FACE,{"disambiguationData":[OSD([sQuery(id+"F0.wireOp",EDGE,"E25.0"),sQuery(id+"F0.wireOp",EDGE,"E25.1"),sQuery(id+"F0.wireOp",EDGE,"E25.2"),sQuery(id+"F0.wireOp",EDGE,"E25.3"),sQuery(id+"F0.wireOp",EDGE,"E25.4"),sQuery(id+"F0.wireOp",EDGE,"E25.5"),sQuery(id+"F0.wireOp",EDGE,"E25.6"),sQuery(id+"F0.wireOp",EDGE,"E25.7")])],"isStart":false})})});
            extrude(context, id + "F13", {"entities" : qUnion([Q0]), "operationType" : NewBodyOperationType.REMOVE, "endBound" : BoundingType.UP_TO_SURFACE, "endBoundEntityFace" : qUnion([Q1]), "depth" : 25 * mm});
        }
        {
            var Q0;
            Q0=makeQuery(id+"F3.boolean.opBoolean","COPY",EDGE,{"derivedFrom":makeQuery(id+"F3.opExtrude","CAP_EDGE",EDGE,{"disambiguationData":[OSD([sQuery(id+"F0.wireOp",EDGE,"E25.6")])],"isStart":false})});
            var Q1;
            Q1=makeQuery(id+"F8.boolean.opBoolean","INTERSECT",EDGE,{"derivedFrom":[makeQuery(id+"F5.opExtrude","SWEPT_FACE",FACE,{"disambiguationData":[OSD([sQuery(id+"F4.wireOp",EDGE,"E30")])]}),makeQuery(id+"F8.opExtrude","CAP_FACE",FACE,{"disambiguationData":[OSD([sQuery(id+"F7.wireOp",EDGE,"E67")])],"isStart":false})]});
            var Q2;
            Q2=makeQuery(id+"F8.boolean.opBoolean","INTERSECT",EDGE,{"disambiguationData":[OD(1.0)],"derivedFrom":[makeQuery(id+"F5.opExtrude","SWEPT_FACE",FACE,{"disambiguationData":[OSD([sQuery(id+"F4.wireOp",EDGE,"E30")])]}),makeQuery(id+"F8.opExtrude","SWEPT_FACE",FACE,{"disambiguationData":[OSD([sQuery(id+"F7.wireOp",EDGE,"E67")])]})]});
            var Q3;
            {var subQ0=sQuery(id+"F4.wireOp",EDGE,"E30");Q3=makeQuery(id+"F8.boolean.opBoolean","SPLIT",EDGE,{"disambiguationData":[TD([makeQuery(id+"F5.opExtrude","SWEPT_FACE",FACE,{"disambiguationData":[OSD([sQuery(id+"F4.wireOp",EDGE,"E35.filletArc")])]})])],"derivedFrom":makeQuery(id+"F5.opExtrude","CAP_EDGE",EDGE,{"disambiguationData":[OSD([subQ0])],"isStart":false})});}
            var Q4;
            {var subQ0=sQuery(id+"F0.wireOp",EDGE,"E25.7");var subQ1=sQuery(id+"F0.wireOp",EDGE,"E25.1");var subQ2=sQuery(id+"F0.wireOp",EDGE,"E25.6");var subQ3=sQuery(id+"F0.wireOp",EDGE,"E25.5");var subQ4=sQuery(id+"F0.wireOp",EDGE,"E25.4");var subQ5=sQuery(id+"F0.wireOp",EDGE,"E25.0");var subQ6=sQuery(id+"F0.wireOp",EDGE,"E25.2");var subQ7=sQuery(id+"F0.wireOp",EDGE,"E25.3");Q4=makeQuery(id+"F8.boolean.opBoolean","INTERSECT",EDGE,{"derivedFrom":[makeQuery(id+"F5.boolean.opBoolean","SPLIT",FACE,{"disambiguationData":[TD([makeQuery(id+"F2.opExtrude","SWEPT_FACE",FACE,{"disambiguationData":[OSD([subQ5])]})])],"derivedFrom":makeQuery(id+"F3.boolean.opBoolean","COPY",FACE,{"derivedFrom":makeQuery(id+"F3.opExtrude","CAP_FACE",FACE,{"disambiguationData":[OSD([subQ5,subQ1,subQ6,subQ7,subQ4,subQ3,subQ2,subQ0])],"isStart":false})})}),makeQuery(id+"F8.opExtrude","SWEPT_FACE",FACE,{"disambiguationData":[OSD([sQuery(id+"F7.wireOp",EDGE,"E67")])]})]});}
            var Q5;
            Q5=makeQuery(id+"F8.boolean.opBoolean","INTERSECT",EDGE,{"disambiguationData":[OD(0.0)],"derivedFrom":[makeQuery(id+"F5.opExtrude","SWEPT_FACE",FACE,{"disambiguationData":[OSD([sQuery(id+"F4.wireOp",EDGE,"E30")])]}),makeQuery(id+"F8.opExtrude","SWEPT_FACE",FACE,{"disambiguationData":[OSD([sQuery(id+"F7.wireOp",EDGE,"E67")])]})]});
            fillet(context, id + "F14", {"entities" : qUnion([Q0, Q1, Q2, Q3, Q4, Q5]), "radius" : 3 * mm, "tangentPropagation" : true, "allowEdgeOverflow" : false});
        }
        {
            var Q0;
            Q0=makeQuery(id+"F1.opExtrude","CAP_EDGE",EDGE,{"disambiguationData":[OSD([sQuery(id+"F0.wireOp",EDGE,"E1.bottom")])],"isStart":false});
            fillet(context, id + "F15", {"entities" : qUnion([Q0]), "radius" : 2 * mm, "tangentPropagation" : true, "allowEdgeOverflow" : false});
        }
        {
            var Q0;
            {var subQ0=sQuery(id+"F0.wireOp",EDGE,"E21.filletArc");var subQ1=sQuery(id+"F0.wireOp",EDGE,"E7");var subQ2=sQuery(id+"F0.wireOp",EDGE,"E6");var subQ3=sQuery(id+"F0.wireOp",EDGE,"E5");var subQ4=sQuery(id+"F0.wireOp",EDGE,"E4");var subQ5=sQuery(id+"F0.wireOp",EDGE,"E22.filletArc");var subQ6=sQuery(id+"F0.wireOp",EDGE,"E1.bottom");var subQ7=sQuery(id+"F0.wireOp",EDGE,"E1.right");var subQ8=sQuery(id+"F0.wireOp",EDGE,"E1.top");var subQ9=sQuery(id+"F0.wireOp",EDGE,"E1.left");var subQ10=sQuery(id+"F0.wireOp",EDGE,"E23.filletArc");var subQ11=sQuery(id+"F0.wireOp",EDGE,"E24.filletArc");Q0=makeQuery(id+"F2.boolean.opBoolean","SPLIT",FACE,{"disambiguationData":[TD([makeQuery(id+"F1.opExtrude","SWEPT_FACE",FACE,{"disambiguationData":[OSD([subQ6])]})])],"derivedFrom":makeQuery(id+"F1.opExtrude","CAP_FACE",FACE,{"disambiguationData":[OSD([subQ6,subQ8,subQ9,subQ7,subQ4,subQ3,subQ2,subQ1,subQ0,subQ5,subQ10,subQ11])],"isStart":true})});}
            var sketch = newSketch(context, id + "F16", { "sketchPlane" : qUnion([Q0])});
            skLineSegment(sketch, "E79.0", {"start": v(-64.25, 74.25) * mm, "end": v(64.25, 74.25) * mm});
            skArc(sketch, "E79.1", {"start": v(74.25, 64.25) * mm, "mid": v(71.32, 71.32) * mm, "end": v(64.25, 74.25) * mm});
            skLineSegment(sketch, "E79.2", {"start": v(74.25, -64.25) * mm, "end": v(74.25, 64.25) * mm});
            skCircle(sketch, "E79.3", {"center": v(60, 60) * mm, "radius": 4 * mm});
            skArc(sketch, "E79.4", {"start": v(54.26, 47.88) * mm, "mid": v(0, 60) * mm, "end": v(-54.26, 47.88) * mm});
            skArc(sketch, "E79.5", {"start": v(60, 38.83) * mm, "mid": v(58.44, 44.2) * mm, "end": v(54.26, 47.88) * mm});
            skLineSegment(sketch, "E79.6", {"start": v(60, 38.83) * mm, "end": v(60, -38.83) * mm});
            skArc(sketch, "E79.7", {"start": v(-64.25, 74.25) * mm, "mid": v(-71.32, 71.32) * mm, "end": v(-74.25, 64.25) * mm});
            skLineSegment(sketch, "E79.8", {"start": v(-74.25, -64.25) * mm, "end": v(-74.25, 64.25) * mm});
            skCircle(sketch, "E79.9", {"center": v(-60, 60) * mm, "radius": 4 * mm});
            skArc(sketch, "E79.10", {"start": v(-54.26, 47.88) * mm, "mid": v(-58.44, 44.2) * mm, "end": v(-60, 38.83) * mm});
            skLineSegment(sketch, "E79.11", {"start": v(-60, 38.83) * mm, "end": v(-60, -38.83) * mm});
            skArc(sketch, "E79.12", {"start": v(-60, -38.83) * mm, "mid": v(-58.44, -44.2) * mm, "end": v(-54.26, -47.88) * mm});
            skArc(sketch, "E79.13", {"start": v(-54.26, -47.88) * mm, "mid": v(0, -60) * mm, "end": v(54.26, -47.88) * mm});
            skArc(sketch, "E79.14", {"start": v(54.26, -47.88) * mm, "mid": v(58.44, -44.2) * mm, "end": v(60, -38.83) * mm});
            skCircle(sketch, "E79.15", {"center": v(60, -60) * mm, "radius": 4 * mm});
            skCircle(sketch, "E79.16", {"center": v(-60, -60) * mm, "radius": 4 * mm});
            skArc(sketch, "E79.17", {"start": v(-74.25, -64.25) * mm, "mid": v(-71.32, -71.32) * mm, "end": v(-64.25, -74.25) * mm});
            skLineSegment(sketch, "E79.18", {"start": v(-64.25, -74.25) * mm, "end": v(64.25, -74.25) * mm});
            skArc(sketch, "E79.19", {"start": v(64.25, -74.25) * mm, "mid": v(71.32, -71.32) * mm, "end": v(74.25, -64.25) * mm});
            skLineSegment(sketch, "E80", {"start": v(0, 74.25) * mm, "end": v(0, 104.25) * mm, "construction": true});
            skPoint(sketch, "E80.endSnap0", {"position": v(0, 74.25) * mm});
            skCircle(sketch, "E81", {"center": v(0, 104.25) * mm, "radius": 6 * mm});
            skLineSegment(sketch, "E82", {"start": v(-33, 74.25) * mm, "end": v(-15, 92.25) * mm});
            skLineSegment(sketch, "E83", {"start": v(-15, 92.25) * mm, "end": v(-15, 104.25) * mm});
            skArc(sketch, "E84", {"start": v(-15, 104.25) * mm, "mid": v(0, 119.25) * mm, "end": v(15, 104.25) * mm});
            skLineSegment(sketch, "E85", {"start": v(15, 104.25) * mm, "end": v(15, 92.25) * mm});
            skLineSegment(sketch, "E86", {"start": v(15, 92.25) * mm, "end": v(33, 74.25) * mm});
            skPoint(sketch, "E87.endSnap0", {"position": v(0, -74.25) * mm});
            skLineSegment(sketch, "E88", {"start": v(0, -74.25) * mm, "end": v(0, -104.25) * mm});
            skCircle(sketch, "E89", {"center": v(0, -104.25) * mm, "radius": 6 * mm});
            skLineSegment(sketch, "E90", {"start": v(-32.64, -74.25) * mm, "end": v(-14.64, -92.25) * mm});
            skLineSegment(sketch, "E91", {"start": v(-14.64, -92.25) * mm, "end": v(-14.64, -104.25) * mm});
            skArc(sketch, "E92", {"start": v(-14.64, -104.25) * mm, "mid": v(0.36, -119.25) * mm, "end": v(15.36, -104.25) * mm});
            skLineSegment(sketch, "E93", {"start": v(33.36, -74.25) * mm, "end": v(15.36, -92.25) * mm});
            skLineSegment(sketch, "E94", {"start": v(15.36, -92.25) * mm, "end": v(15.36, -104.25) * mm});
            skSolve(sketch);
        }
        {
            var Q0;
            Q0 = qSketchRegion(id + "F16", true);
            var Q1;
            Q1=sQuery(id+"F16.wireOp",EDGE,"E84");
            var Q2;
            Q2=sQuery(id+"F16.wireOp",EDGE,"E83");
            var Q3;
            Q3=sQuery(id+"F16.wireOp",EDGE,"E82");
            var Q4;
            Q4=sQuery(id+"F16.wireOp",EDGE,"E86");
            var Q5;
            Q5=sQuery(id+"F16.wireOp",EDGE,"E85");
            var Q6;
            Q6 = qConstructionFilter(qBodyType(qCreatedBy(id + "F4" ,EDGE), BodyType.WIRE), ConstructionObject.NO);
            extrude(context, id + "F17", {"entities" : qUnion([Q0]), "bodyType" : ToolBodyType.SURFACE, "surfaceEntities" : qUnion([Q1, Q2, Q3, Q4, Q5, Q6]), "depth" : 25 * mm});
        }
        {
            var Q0;
            Q0=makeQuery(id+"F16.imprint","IMPRINT",FACE,{"disambiguationData":[TD([[makeQuery(id+"F16.imprint","IMPRINT",EDGE,{"derivedFrom":sQuery(id+"F16.wireOp",EDGE,"E89")}),-1.0]])]});
            var Q1;
            Q1=makeQuery(id+"F16.imprint","IMPRINT",FACE,{"disambiguationData":[TD([[makeQuery(id+"F16.imprint","IMPRINT",EDGE,{"derivedFrom":sQuery(id+"F16.wireOp",EDGE,"E81")}),-1.0]])]});
            extrude(context, id + "F18", {"entities" : qUnion([Q0, Q1]), "operationType" : NewBodyOperationType.ADD, "depth" : 25 * mm});
        }
    });
